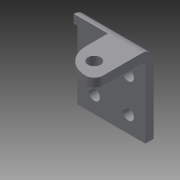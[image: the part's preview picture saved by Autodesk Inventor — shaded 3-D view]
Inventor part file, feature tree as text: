
AUTODESK INVENTOR PART (.ipt)
format: ipt  version: 2014 (Build 180170000, 170)  size: 172,032 bytes
history: native  units: in
note: dims shown in document units (in); Inventor stores cm internally (conversion verified against a paired STEP export)
features: sheet_metal_op x4, sketch x3, other x3, extrude x1, fillet x1
ambient origin geometry x8: Origin, YZ Plane, XZ Plane, XY Plane, X Axis, Y Axis, Z Axis, Center Point
bodies: Solid1 (feature_tree)
feature tree (12):
  sheet_metal_op  "Face1"
  sheet_metal_op  "Flange1"
  extrude  "Extrusion1"  Depth=1.0in
  fillet  "Fillet1"  Radius=0.164in
  sketch  "Sketch1"  dims[d0=1.0in d1=1.0in d2=0.164in]
  other  "Plate1"
  sketch  "Sketch2"  dims[d3=0.25in]
  other  "Plate2"
  sheet_metal_op  "Bend1"
  sheet_metal_op  "Corner1"
  sketch  "Sketch3"  dims[d4=0.25in d5=0.7874in d7=0.5in d8=0.7874in d10=0.5in d13=0.125in d14=0.125in d15=0.0625in d16=0.25in d17=0.125in d18=0.875in d19=90.0deg d20=0.05in d21=0.5in d22=0.125in d23=0.125in d24=0.187in d25=0.25in d26=0.25in d27=0.375in d28=0.125in d29=0.5in d30=1.0in d31=0.0in d32=0.125in]
  other  "Definition1"
